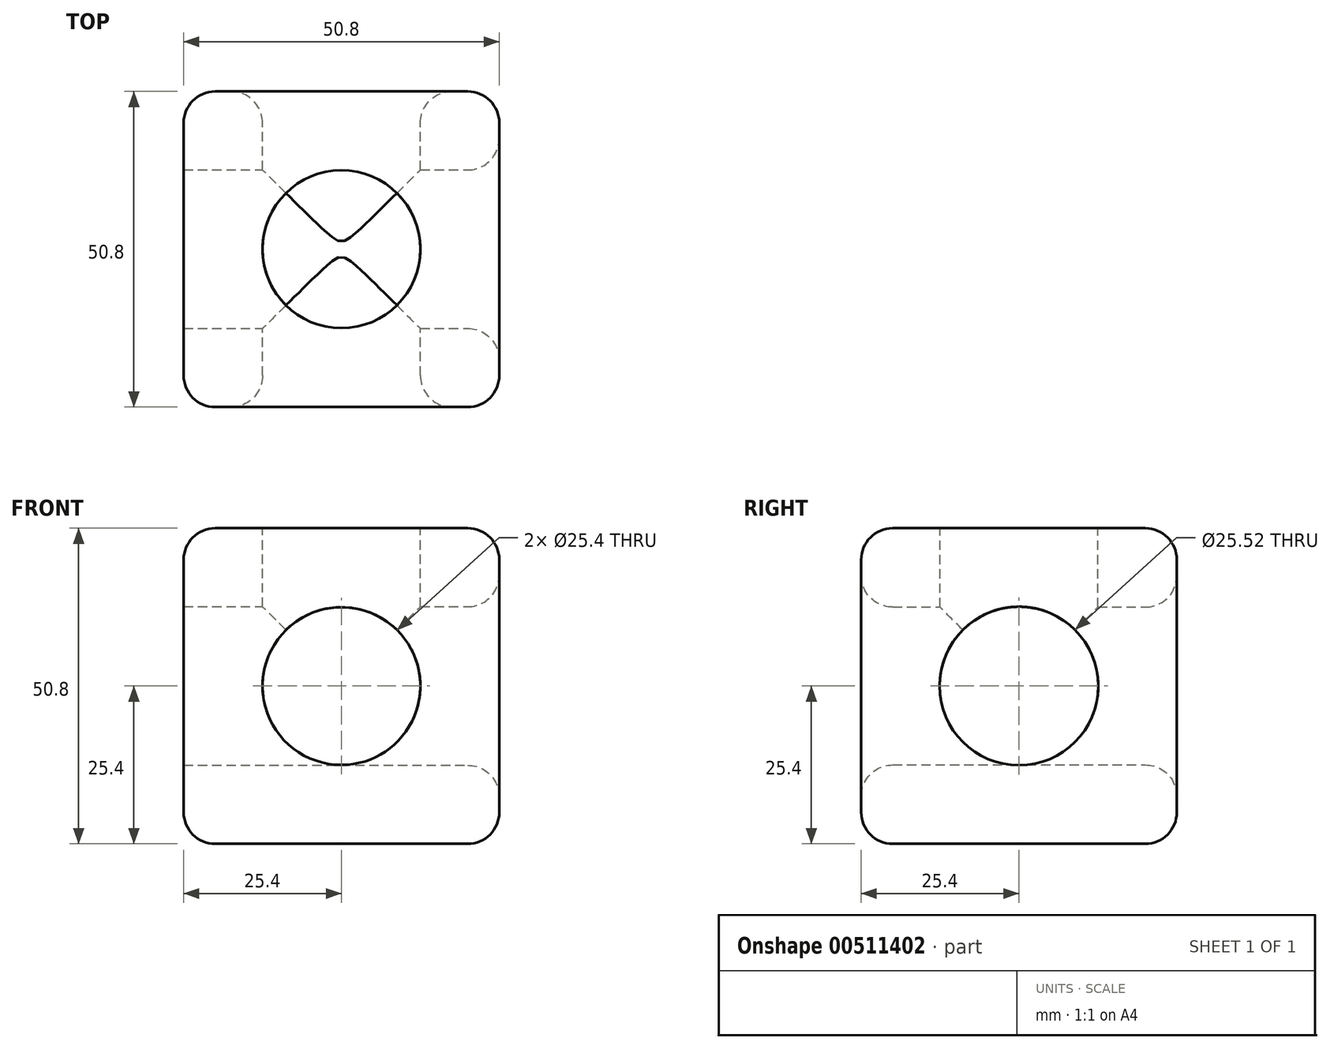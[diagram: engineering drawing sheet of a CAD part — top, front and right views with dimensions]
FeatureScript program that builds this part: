
annotation { "Feature Type Name" : "Feature", "Feature Type Description" : "" }
export const myFeature = defineFeature(function(context is Context, id is Id, definition is map)
    precondition{}
    {
        {
            var Q0;
            Q0=qCreatedBy(makeId("Front.planeOp"),FACE);
            var sketch = newSketch(context, id + "F0", { "sketchPlane" : qUnion([Q0])});
            skLineSegment(sketch, "E0", {"start": v(0, 0) * mm, "end": v(0, 50.8) * mm});
            skLineSegment(sketch, "E1", {"start": v(0, 0) * mm, "end": v(50.8, 0) * mm});
            skLineSegment(sketch, "E2", {"start": v(50.8, 0) * mm, "end": v(50.8, 50.8) * mm});
            skLineSegment(sketch, "E3", {"start": v(0, 50.8) * mm, "end": v(50.8, 50.8) * mm});
            skLineSegment(sketch, "E4", {"start": v(0, 50.8) * mm, "end": v(50.8, 0) * mm});
            skLineSegment(sketch, "E5", {"start": v(50.8, 50.8) * mm, "end": v(0, 0) * mm});
            skCircle(sketch, "E6", {"center": v(25.4, 25.4) * mm, "radius": 12.7 * mm});
            skSolve(sketch);
        }
        {
            var Q0;
            Q0=makeQuery(id+"F0.imprint","IMPRINT",FACE,{"disambiguationData":[TD([[makeQuery(id+"F0.imprint","IMPRINT",EDGE,{"derivedFrom":sQuery(id+"F0.wireOp",EDGE,"E0")}),-1.0]])]});
            var Q1;
            {var subQ0=sQuery(id+"F0.wireOp",EDGE,"E3");Q1=makeQuery(id+"F0.imprint","IMPRINT",FACE,{"disambiguationData":[TD([[makeQuery(id+"F0.imprint","IMPRINT",EDGE,{"derivedFrom":subQ0}),-1.0]])]});}
            var Q2;
            {var subQ0=sQuery(id+"F0.wireOp",EDGE,"E2");Q2=makeQuery(id+"F0.imprint","IMPRINT",FACE,{"disambiguationData":[TD([[makeQuery(id+"F0.imprint","IMPRINT",EDGE,{"derivedFrom":subQ0}),1.0]])]});}
            var Q3;
            {var subQ0=sQuery(id+"F0.wireOp",EDGE,"E1");Q3=makeQuery(id+"F0.imprint","IMPRINT",FACE,{"disambiguationData":[TD([[makeQuery(id+"F0.imprint","IMPRINT",EDGE,{"derivedFrom":subQ0}),1.0]])]});}
            extrude(context, id + "F1", {"entities" : qUnion([Q0, Q1, Q2, Q3]), "depth" : 50.8 * mm, "offsetDistance" : 25.4 * mm});
        }
        {
            var Q0;
            Q0=makeQuery(id+"F1.opExtrude","SWEPT_FACE",FACE,{"disambiguationData":[OSD([sQuery(id+"F0.wireOp",EDGE,"E3")])]});
            var sketch = newSketch(context, id + "F2", { "sketchPlane" : qUnion([Q0])});
            skLineSegment(sketch, "E7", {"start": v(50.8, 0) * mm, "end": v(0, -50.8) * mm});
            skLineSegment(sketch, "E8", {"start": v(50.8, -50.8) * mm, "end": v(0, 0) * mm});
            skCircle(sketch, "E9", {"center": v(25.4, -25.4) * mm, "radius": 12.7 * mm});
            skSolve(sketch);
        }
        {
            var Q0;
            Q0=makeQuery(id+"F1.opExtrude","SWEPT_FACE",FACE,{"disambiguationData":[OSD([sQuery(id+"F0.wireOp",EDGE,"E2")])]});
            var sketch = newSketch(context, id + "F3", { "sketchPlane" : qUnion([Q0])});
            skCircle(sketch, "E10", {"center": v(-25.4, 25.4) * mm, "radius": 12.76 * mm});
            skSolve(sketch);
        }
        {
            var Q0;
            Q0=makeQuery(id+"F3.imprint","IMPRINT",FACE,{"disambiguationData":[TD([[makeQuery(id+"F3.imprint","IMPRINT",EDGE,{"derivedFrom":sQuery(id+"F3.wireOp",EDGE,"E10")}),1.0]])]});
            extrude(context, id + "F4", {"entities" : qUnion([Q0]), "operationType" : NewBodyOperationType.REMOVE, "oppositeDirection" : true, "depth" : 50.8 * mm, "offsetDistance" : 25.4 * mm});
        }
        {
            var Q0;
            Q0 = qSketchRegion(id + "F2", true);
            extrude(context, id + "F5", {"entities" : qUnion([Q0]), "operationType" : NewBodyOperationType.REMOVE, "oppositeDirection" : true, "depth" : 25.4 * mm, "offsetDistance" : 25.4 * mm});
        }
        {
            var Q0;
            Q0=makeQuery(id+"F1.opExtrude","SWEPT_EDGE",EDGE,{"disambiguationData":[OSD([sQuery(id+"F0.wireOp",EDGE,"E0"),sQuery(id+"F0.wireOp",EDGE,"E3"),sQuery(id+"F0.wireOp",EDGE,"E4")])]});
            var Q1;
            Q1=makeQuery(id+"F1.opExtrude","CAP_EDGE",EDGE,{"disambiguationData":[OSD([sQuery(id+"F0.wireOp",EDGE,"E0")])],"isStart":false});
            var Q2;
            Q2=makeQuery(id+"F1.opExtrude","CAP_EDGE",EDGE,{"disambiguationData":[OSD([sQuery(id+"F0.wireOp",EDGE,"E2")])],"isStart":false});
            var Q3;
            Q3=makeQuery(id+"F1.opExtrude","CAP_EDGE",EDGE,{"disambiguationData":[OSD([sQuery(id+"F0.wireOp",EDGE,"E2")])],"isStart":true});
            var Q4;
            Q4=makeQuery(id+"F1.opExtrude","SWEPT_EDGE",EDGE,{"disambiguationData":[OSD([sQuery(id+"F0.wireOp",EDGE,"E2"),sQuery(id+"F0.wireOp",EDGE,"E3"),sQuery(id+"F0.wireOp",EDGE,"E5")])]});
            var Q5;
            Q5=makeQuery(id+"F1.opExtrude","SWEPT_FACE",FACE,{"disambiguationData":[OSD([sQuery(id+"F0.wireOp",EDGE,"E2")])]});
            var Q6;
            Q6=makeQuery(id+"F1.opExtrude","CAP_FACE",FACE,{"disambiguationData":[OSD([sQuery(id+"F0.wireOp",EDGE,"E0"),sQuery(id+"F0.wireOp",EDGE,"E1"),sQuery(id+"F0.wireOp",EDGE,"E2"),sQuery(id+"F0.wireOp",EDGE,"E3"),sQuery(id+"F0.wireOp",EDGE,"E6")])],"isStart":false});
            var Q7;
            Q7=makeQuery(id+"F1.opExtrude","SWEPT_EDGE",EDGE,{"disambiguationData":[OSD([sQuery(id+"F0.wireOp",EDGE,"E0"),sQuery(id+"F0.wireOp",EDGE,"E1"),sQuery(id+"F0.wireOp",EDGE,"E5")])]});
            var Q8;
            Q8=makeQuery(id+"F1.opExtrude","CAP_EDGE",EDGE,{"disambiguationData":[OSD([sQuery(id+"F0.wireOp",EDGE,"E0")])],"isStart":true});
            var Q9;
            Q9=makeQuery(id+"F1.opExtrude","CAP_EDGE",EDGE,{"disambiguationData":[OSD([sQuery(id+"F0.wireOp",EDGE,"E3")])],"isStart":true});
            var Q10;
            Q10=makeQuery(id+"F1.opExtrude","CAP_FACE",FACE,{"disambiguationData":[OSD([sQuery(id+"F0.wireOp",EDGE,"E0"),sQuery(id+"F0.wireOp",EDGE,"E1"),sQuery(id+"F0.wireOp",EDGE,"E2"),sQuery(id+"F0.wireOp",EDGE,"E3"),sQuery(id+"F0.wireOp",EDGE,"E6")])],"isStart":true});
            var Q11;
            Q11=makeQuery(id+"F1.opExtrude","CAP_EDGE",EDGE,{"disambiguationData":[OSD([sQuery(id+"F0.wireOp",EDGE,"E1")])],"isStart":true});
            fillet(context, id + "F6", {"entities" : qUnion([Q0, Q1, Q2, Q3, Q4, Q5, Q6, Q7, Q8, Q9, Q10, Q11]), "radius" : 5.08 * mm, "tangentPropagation" : true, "allowEdgeOverflow" : false});
        }
    });
